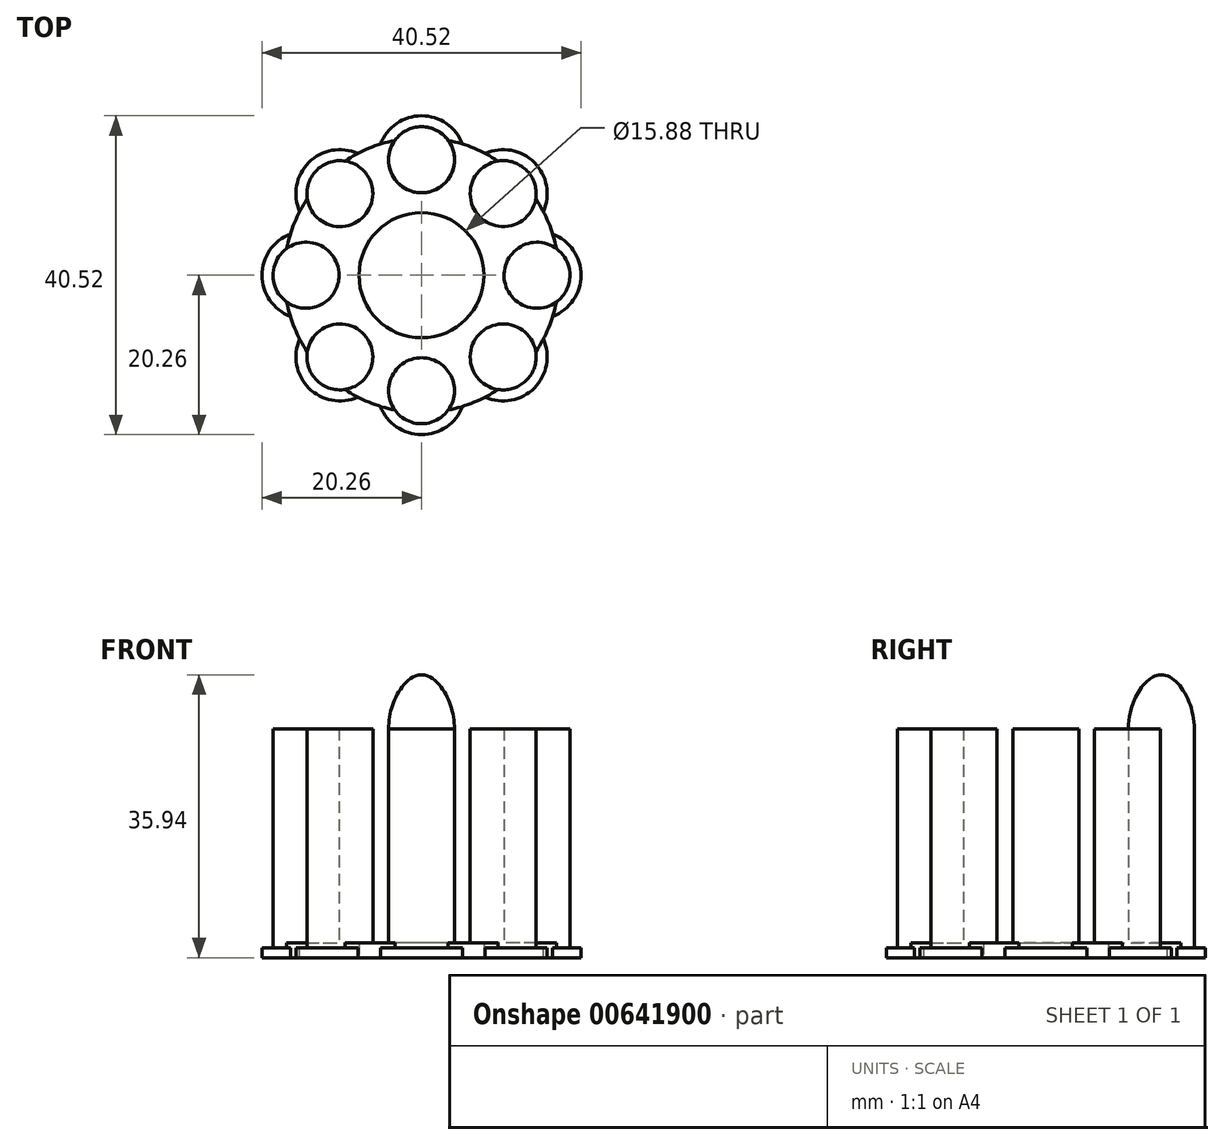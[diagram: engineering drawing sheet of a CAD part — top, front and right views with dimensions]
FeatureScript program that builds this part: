
annotation { "Feature Type Name" : "Feature", "Feature Type Description" : "" }
export const myFeature = defineFeature(function(context is Context, id is Id, definition is map)
    precondition{}
    {
        {
            var Q0;
            Q0=qCreatedBy(makeId("Top.planeOp"),FACE);
            var sketch = newSketch(context, id + "F0", { "sketchPlane" : qUnion([Q0])});
            skCircle(sketch, "E0", {"center": v(0, 14.67) * mm, "radius": 5.59 * mm});
            skCircle(sketch, "E1", {"center": v(0, 0) * mm, "radius": 7.94 * mm});
            skCircle(sketch, "E2", {"center": v(0, 14.67) * mm, "radius": 4.2 * mm});
            skCircle(sketch, "E3", {"center": v(0, 0) * mm, "radius": 17.46 * mm});
            skCircle(sketch, "E4.1.0", {"center": v(-10.37, 10.37) * mm, "radius": 4.2 * mm});
            skCircle(sketch, "E4.1.1", {"center": v(-10.37, 10.37) * mm, "radius": 5.59 * mm});
            skCircle(sketch, "E4.2.0", {"center": v(-14.67, 0) * mm, "radius": 4.2 * mm});
            skCircle(sketch, "E4.2.1", {"center": v(-14.67, 0) * mm, "radius": 5.59 * mm});
            skCircle(sketch, "E5.1.3.0", {"center": v(-10.37, -10.37) * mm, "radius": 4.2 * mm});
            skCircle(sketch, "E5.2.3.0", {"center": v(-10.37, -10.37) * mm, "radius": 5.59 * mm});
            skCircle(sketch, "E5.1.4.0", {"center": v(0, -14.67) * mm, "radius": 4.2 * mm});
            skCircle(sketch, "E5.2.4.0", {"center": v(0, -14.67) * mm, "radius": 5.59 * mm});
            skCircle(sketch, "E5.1.5.0", {"center": v(10.37, -10.37) * mm, "radius": 4.2 * mm});
            skCircle(sketch, "E5.2.5.0", {"center": v(10.37, -10.37) * mm, "radius": 5.59 * mm});
            skCircle(sketch, "E5.1.6.0", {"center": v(14.67, 0) * mm, "radius": 4.2 * mm});
            skCircle(sketch, "E5.2.6.0", {"center": v(14.67, 0) * mm, "radius": 5.59 * mm});
            skCircle(sketch, "E5.1.7.0", {"center": v(10.37, 10.37) * mm, "radius": 4.2 * mm});
            skCircle(sketch, "E5.2.7.0", {"center": v(10.37, 10.37) * mm, "radius": 5.59 * mm});
            skSolve(sketch);
        }
        {
            var Q0;
            {var subQ0=sQuery(id+"F0.wireOp",EDGE,"E3");var subQ1=sQuery(id+"F0.wireOp",EDGE,"E0");var subQ2=makeQuery(id+"F0.imprint","INTERSECT",VERTEX,{"disambiguationData":[OD(0.0)],"derivedFrom":[subQ1,subQ0]});Q0=makeQuery(id+"F0.imprint","IMPRINT",FACE,{"disambiguationData":[TD([[makeQuery(id+"F0.imprint","IMPRINT",EDGE,{"disambiguationData":[TD([[subQ2,1.0]])],"derivedFrom":subQ1}),1.0]])]});}
            var Q1;
            {var subQ0=sQuery(id+"F0.wireOp",EDGE,"E5.2.7.0");var subQ1=sQuery(id+"F0.wireOp",EDGE,"E3");var subQ2=makeQuery(id+"F0.imprint","INTERSECT",VERTEX,{"disambiguationData":[OD(0.0)],"derivedFrom":[subQ1,subQ0]});Q1=makeQuery(id+"F0.imprint","IMPRINT",FACE,{"disambiguationData":[TD([[makeQuery(id+"F0.imprint","IMPRINT",EDGE,{"disambiguationData":[TD([[subQ2,-1.0]])],"derivedFrom":subQ1}),1.0]])]});}
            var Q2;
            {var subQ0=sQuery(id+"F0.wireOp",EDGE,"E5.2.6.0");var subQ1=sQuery(id+"F0.wireOp",EDGE,"E3");var subQ2=makeQuery(id+"F0.imprint","INTERSECT",VERTEX,{"disambiguationData":[OD(0.0)],"derivedFrom":[subQ1,subQ0]});Q2=makeQuery(id+"F0.imprint","IMPRINT",FACE,{"disambiguationData":[TD([[makeQuery(id+"F0.imprint","IMPRINT",EDGE,{"disambiguationData":[TD([[subQ2,1.0]])],"derivedFrom":subQ1}),1.0]])]});}
            var Q3;
            {var subQ0=sQuery(id+"F0.wireOp",EDGE,"E5.2.5.0");var subQ1=sQuery(id+"F0.wireOp",EDGE,"E3");var subQ2=makeQuery(id+"F0.imprint","INTERSECT",VERTEX,{"disambiguationData":[OD(0.0)],"derivedFrom":[subQ1,subQ0]});Q3=makeQuery(id+"F0.imprint","IMPRINT",FACE,{"disambiguationData":[TD([[makeQuery(id+"F0.imprint","IMPRINT",EDGE,{"disambiguationData":[TD([[subQ2,-1.0]])],"derivedFrom":subQ1}),1.0]])]});}
            var Q4;
            {var subQ0=sQuery(id+"F0.wireOp",EDGE,"E5.2.4.0");var subQ1=sQuery(id+"F0.wireOp",EDGE,"E3");var subQ2=makeQuery(id+"F0.imprint","INTERSECT",VERTEX,{"disambiguationData":[OD(0.0)],"derivedFrom":[subQ1,subQ0]});Q4=makeQuery(id+"F0.imprint","IMPRINT",FACE,{"disambiguationData":[TD([[makeQuery(id+"F0.imprint","IMPRINT",EDGE,{"disambiguationData":[TD([[subQ2,-1.0]])],"derivedFrom":subQ1}),1.0]])]});}
            var Q5;
            {var subQ0=sQuery(id+"F0.wireOp",EDGE,"E5.2.3.0");var subQ1=sQuery(id+"F0.wireOp",EDGE,"E3");var subQ2=makeQuery(id+"F0.imprint","INTERSECT",VERTEX,{"disambiguationData":[OD(0.0)],"derivedFrom":[subQ1,subQ0]});Q5=makeQuery(id+"F0.imprint","IMPRINT",FACE,{"disambiguationData":[TD([[makeQuery(id+"F0.imprint","IMPRINT",EDGE,{"disambiguationData":[TD([[subQ2,-1.0]])],"derivedFrom":subQ1}),1.0]])]});}
            var Q6;
            {var subQ0=sQuery(id+"F0.wireOp",EDGE,"E4.2.1");var subQ1=sQuery(id+"F0.wireOp",EDGE,"E3");var subQ2=makeQuery(id+"F0.imprint","INTERSECT",VERTEX,{"disambiguationData":[OD(0.0)],"derivedFrom":[subQ1,subQ0]});Q6=makeQuery(id+"F0.imprint","IMPRINT",FACE,{"disambiguationData":[TD([[makeQuery(id+"F0.imprint","IMPRINT",EDGE,{"disambiguationData":[TD([[subQ2,-1.0]])],"derivedFrom":subQ1}),1.0]])]});}
            var Q7;
            {var subQ0=sQuery(id+"F0.wireOp",EDGE,"E4.1.1");var subQ1=sQuery(id+"F0.wireOp",EDGE,"E3");var subQ2=makeQuery(id+"F0.imprint","INTERSECT",VERTEX,{"disambiguationData":[OD(0.0)],"derivedFrom":[subQ1,subQ0]});Q7=makeQuery(id+"F0.imprint","IMPRINT",FACE,{"disambiguationData":[TD([[makeQuery(id+"F0.imprint","IMPRINT",EDGE,{"disambiguationData":[TD([[subQ2,-1.0]])],"derivedFrom":subQ1}),1.0]])]});}
            var Q8;
            Q8=makeQuery(id+"F0.imprint","IMPRINT",FACE,{"disambiguationData":[TD([[makeQuery(id+"F0.imprint","IMPRINT",EDGE,{"derivedFrom":sQuery(id+"F0.wireOp",EDGE,"E1")}),-1.0]])]});
            extrude(context, id + "F1", {"entities" : qUnion([Q0, Q1, Q2, Q3, Q4, Q5, Q6, Q7, Q8]), "depth" : 0.64 * mm, "offsetDistance" : 25.4 * mm});
        }
        {
            var Q0;
            Q0 = qSketchRegion(id + "F0", true);
            var Q1;
            {var subQ0=sQuery(id+"F0.wireOp",EDGE,"E5.1.4.0");var subQ1=sQuery(id+"F0.wireOp",EDGE,"E3");var subQ2=makeQuery(id+"F0.imprint","INTERSECT",VERTEX,{"disambiguationData":[OD(0.0)],"derivedFrom":[subQ1,subQ0]});Q1=makeQuery(id+"F0.imprint","IMPRINT",FACE,{"disambiguationData":[TD([[makeQuery(id+"F0.imprint","IMPRINT",EDGE,{"disambiguationData":[TD([[subQ2,-1.0]])],"derivedFrom":subQ1}),-1.0]])]});}
            var Q2;
            {var subQ0=sQuery(id+"F0.wireOp",EDGE,"E5.1.4.0");var subQ1=sQuery(id+"F0.wireOp",EDGE,"E3");var subQ2=makeQuery(id+"F0.imprint","INTERSECT",VERTEX,{"disambiguationData":[OD(0.0)],"derivedFrom":[subQ1,subQ0]});Q2=makeQuery(id+"F0.imprint","IMPRINT",FACE,{"disambiguationData":[TD([[makeQuery(id+"F0.imprint","IMPRINT",EDGE,{"disambiguationData":[TD([[subQ2,-1.0]])],"derivedFrom":subQ1}),1.0]])]});}
            var Q3;
            {var subQ0=sQuery(id+"F0.wireOp",EDGE,"E5.1.5.0");var subQ1=sQuery(id+"F0.wireOp",EDGE,"E3");var subQ2=makeQuery(id+"F0.imprint","INTERSECT",VERTEX,{"disambiguationData":[OD(0.0)],"derivedFrom":[subQ1,subQ0]});Q3=makeQuery(id+"F0.imprint","IMPRINT",FACE,{"disambiguationData":[TD([[makeQuery(id+"F0.imprint","IMPRINT",EDGE,{"disambiguationData":[TD([[subQ2,-1.0]])],"derivedFrom":subQ1}),1.0]])]});}
            var Q4;
            {var subQ0=sQuery(id+"F0.wireOp",EDGE,"E5.1.5.0");var subQ1=sQuery(id+"F0.wireOp",EDGE,"E3");var subQ2=makeQuery(id+"F0.imprint","INTERSECT",VERTEX,{"disambiguationData":[OD(0.0)],"derivedFrom":[subQ1,subQ0]});Q4=makeQuery(id+"F0.imprint","IMPRINT",FACE,{"disambiguationData":[TD([[makeQuery(id+"F0.imprint","IMPRINT",EDGE,{"disambiguationData":[TD([[subQ2,-1.0]])],"derivedFrom":subQ1}),-1.0]])]});}
            var Q5;
            {var subQ0=sQuery(id+"F0.wireOp",EDGE,"E5.1.6.0");var subQ1=sQuery(id+"F0.wireOp",EDGE,"E3");var subQ2=makeQuery(id+"F0.imprint","INTERSECT",VERTEX,{"disambiguationData":[OD(0.0)],"derivedFrom":[subQ1,subQ0]});Q5=makeQuery(id+"F0.imprint","IMPRINT",FACE,{"disambiguationData":[TD([[makeQuery(id+"F0.imprint","IMPRINT",EDGE,{"disambiguationData":[TD([[subQ2,1.0]])],"derivedFrom":subQ1}),-1.0]])]});}
            var Q6;
            {var subQ0=sQuery(id+"F0.wireOp",EDGE,"E5.1.6.0");var subQ1=sQuery(id+"F0.wireOp",EDGE,"E3");var subQ2=makeQuery(id+"F0.imprint","INTERSECT",VERTEX,{"disambiguationData":[OD(0.0)],"derivedFrom":[subQ1,subQ0]});Q6=makeQuery(id+"F0.imprint","IMPRINT",FACE,{"disambiguationData":[TD([[makeQuery(id+"F0.imprint","IMPRINT",EDGE,{"disambiguationData":[TD([[subQ2,1.0]])],"derivedFrom":subQ1}),1.0]])]});}
            var Q7;
            {var subQ0=sQuery(id+"F0.wireOp",EDGE,"E5.1.7.0");var subQ1=sQuery(id+"F0.wireOp",EDGE,"E3");var subQ2=makeQuery(id+"F0.imprint","INTERSECT",VERTEX,{"disambiguationData":[OD(0.0)],"derivedFrom":[subQ1,subQ0]});Q7=makeQuery(id+"F0.imprint","IMPRINT",FACE,{"disambiguationData":[TD([[makeQuery(id+"F0.imprint","IMPRINT",EDGE,{"disambiguationData":[TD([[subQ2,-1.0]])],"derivedFrom":subQ1}),1.0]])]});}
            var Q8;
            {var subQ0=sQuery(id+"F0.wireOp",EDGE,"E5.1.7.0");var subQ1=sQuery(id+"F0.wireOp",EDGE,"E3");var subQ2=makeQuery(id+"F0.imprint","INTERSECT",VERTEX,{"disambiguationData":[OD(0.0)],"derivedFrom":[subQ1,subQ0]});Q8=makeQuery(id+"F0.imprint","IMPRINT",FACE,{"disambiguationData":[TD([[makeQuery(id+"F0.imprint","IMPRINT",EDGE,{"disambiguationData":[TD([[subQ2,-1.0]])],"derivedFrom":subQ1}),-1.0]])]});}
            var Q9;
            {var subQ0=sQuery(id+"F0.wireOp",EDGE,"E4.1.0");var subQ1=sQuery(id+"F0.wireOp",EDGE,"E3");var subQ2=makeQuery(id+"F0.imprint","INTERSECT",VERTEX,{"disambiguationData":[OD(0.0)],"derivedFrom":[subQ1,subQ0]});Q9=makeQuery(id+"F0.imprint","IMPRINT",FACE,{"disambiguationData":[TD([[makeQuery(id+"F0.imprint","IMPRINT",EDGE,{"disambiguationData":[TD([[subQ2,-1.0]])],"derivedFrom":subQ1}),1.0]])]});}
            var Q10;
            {var subQ0=sQuery(id+"F0.wireOp",EDGE,"E4.1.0");var subQ1=sQuery(id+"F0.wireOp",EDGE,"E3");var subQ2=makeQuery(id+"F0.imprint","INTERSECT",VERTEX,{"disambiguationData":[OD(0.0)],"derivedFrom":[subQ1,subQ0]});Q10=makeQuery(id+"F0.imprint","IMPRINT",FACE,{"disambiguationData":[TD([[makeQuery(id+"F0.imprint","IMPRINT",EDGE,{"disambiguationData":[TD([[subQ2,-1.0]])],"derivedFrom":subQ1}),-1.0]])]});}
            var Q11;
            {var subQ0=sQuery(id+"F0.wireOp",EDGE,"E4.2.0");var subQ1=sQuery(id+"F0.wireOp",EDGE,"E3");var subQ2=makeQuery(id+"F0.imprint","INTERSECT",VERTEX,{"disambiguationData":[OD(0.0)],"derivedFrom":[subQ1,subQ0]});Q11=makeQuery(id+"F0.imprint","IMPRINT",FACE,{"disambiguationData":[TD([[makeQuery(id+"F0.imprint","IMPRINT",EDGE,{"disambiguationData":[TD([[subQ2,-1.0]])],"derivedFrom":subQ1}),1.0]])]});}
            var Q12;
            {var subQ0=sQuery(id+"F0.wireOp",EDGE,"E3");var subQ1=sQuery(id+"F0.wireOp",EDGE,"E2");var subQ2=makeQuery(id+"F0.imprint","INTERSECT",VERTEX,{"disambiguationData":[OD(0.0)],"derivedFrom":[subQ1,subQ0]});Q12=makeQuery(id+"F0.imprint","IMPRINT",FACE,{"disambiguationData":[TD([[makeQuery(id+"F0.imprint","IMPRINT",EDGE,{"disambiguationData":[TD([[subQ2,1.0]])],"derivedFrom":subQ1}),1.0]])]});}
            var Q13;
            {var subQ0=sQuery(id+"F0.wireOp",EDGE,"E3");var subQ1=sQuery(id+"F0.wireOp",EDGE,"E2");var subQ2=makeQuery(id+"F0.imprint","INTERSECT",VERTEX,{"disambiguationData":[OD(0.0)],"derivedFrom":[subQ1,subQ0]});Q13=makeQuery(id+"F0.imprint","IMPRINT",FACE,{"disambiguationData":[TD([[makeQuery(id+"F0.imprint","IMPRINT",EDGE,{"disambiguationData":[TD([[subQ2,-1.0]])],"derivedFrom":subQ1}),1.0]])]});}
            var Q14;
            {var subQ0=sQuery(id+"F0.wireOp",EDGE,"E5.1.3.0");var subQ1=sQuery(id+"F0.wireOp",EDGE,"E3");var subQ2=makeQuery(id+"F0.imprint","INTERSECT",VERTEX,{"disambiguationData":[OD(0.0)],"derivedFrom":[subQ1,subQ0]});Q14=makeQuery(id+"F0.imprint","IMPRINT",FACE,{"disambiguationData":[TD([[makeQuery(id+"F0.imprint","IMPRINT",EDGE,{"disambiguationData":[TD([[subQ2,-1.0]])],"derivedFrom":subQ1}),-1.0]])]});}
            var Q15;
            {var subQ0=sQuery(id+"F0.wireOp",EDGE,"E5.1.3.0");var subQ1=sQuery(id+"F0.wireOp",EDGE,"E3");var subQ2=makeQuery(id+"F0.imprint","INTERSECT",VERTEX,{"disambiguationData":[OD(0.0)],"derivedFrom":[subQ1,subQ0]});Q15=makeQuery(id+"F0.imprint","IMPRINT",FACE,{"disambiguationData":[TD([[makeQuery(id+"F0.imprint","IMPRINT",EDGE,{"disambiguationData":[TD([[subQ2,-1.0]])],"derivedFrom":subQ1}),1.0]])]});}
            var Q16;
            {var subQ0=sQuery(id+"F0.wireOp",EDGE,"E4.2.0");var subQ1=sQuery(id+"F0.wireOp",EDGE,"E3");var subQ2=makeQuery(id+"F0.imprint","INTERSECT",VERTEX,{"disambiguationData":[OD(0.0)],"derivedFrom":[subQ1,subQ0]});Q16=makeQuery(id+"F0.imprint","IMPRINT",FACE,{"disambiguationData":[TD([[makeQuery(id+"F0.imprint","IMPRINT",EDGE,{"disambiguationData":[TD([[subQ2,-1.0]])],"derivedFrom":subQ1}),-1.0]])]});}
            extrude(context, id + "F2", {"entities" : qUnion([Q0, Q1, Q2, Q3, Q4, Q5, Q6, Q7, Q8, Q9, Q10, Q11, Q12, Q13, Q14, Q15, Q16]), "operationType" : NewBodyOperationType.ADD, "oppositeDirection" : true, "depth" : 1.27 * mm, "offsetDistance" : 25.4 * mm});
        }
        {
            var Q0;
            {var subQ0=sQuery(id+"F0.wireOp",EDGE,"E5.1.5.0");var subQ1=sQuery(id+"F0.wireOp",EDGE,"E3");var subQ2=makeQuery(id+"F0.imprint","INTERSECT",VERTEX,{"disambiguationData":[OD(0.0)],"derivedFrom":[subQ1,subQ0]});Q0=makeQuery(id+"F0.imprint","IMPRINT",FACE,{"disambiguationData":[TD([[makeQuery(id+"F0.imprint","IMPRINT",EDGE,{"disambiguationData":[TD([[subQ2,-1.0]])],"derivedFrom":subQ1}),1.0]])]});}
            var Q1;
            {var subQ0=sQuery(id+"F0.wireOp",EDGE,"E5.1.5.0");var subQ1=sQuery(id+"F0.wireOp",EDGE,"E3");var subQ2=makeQuery(id+"F0.imprint","INTERSECT",VERTEX,{"disambiguationData":[OD(0.0)],"derivedFrom":[subQ1,subQ0]});Q1=makeQuery(id+"F0.imprint","IMPRINT",FACE,{"disambiguationData":[TD([[makeQuery(id+"F0.imprint","IMPRINT",EDGE,{"disambiguationData":[TD([[subQ2,-1.0]])],"derivedFrom":subQ1}),-1.0]])]});}
            var Q2;
            {var subQ0=sQuery(id+"F0.wireOp",EDGE,"E5.1.4.0");var subQ1=sQuery(id+"F0.wireOp",EDGE,"E3");var subQ2=makeQuery(id+"F0.imprint","INTERSECT",VERTEX,{"disambiguationData":[OD(0.0)],"derivedFrom":[subQ1,subQ0]});Q2=makeQuery(id+"F0.imprint","IMPRINT",FACE,{"disambiguationData":[TD([[makeQuery(id+"F0.imprint","IMPRINT",EDGE,{"disambiguationData":[TD([[subQ2,-1.0]])],"derivedFrom":subQ1}),-1.0]])]});}
            var Q3;
            {var subQ0=sQuery(id+"F0.wireOp",EDGE,"E5.1.4.0");var subQ1=sQuery(id+"F0.wireOp",EDGE,"E3");var subQ2=makeQuery(id+"F0.imprint","INTERSECT",VERTEX,{"disambiguationData":[OD(0.0)],"derivedFrom":[subQ1,subQ0]});Q3=makeQuery(id+"F0.imprint","IMPRINT",FACE,{"disambiguationData":[TD([[makeQuery(id+"F0.imprint","IMPRINT",EDGE,{"disambiguationData":[TD([[subQ2,-1.0]])],"derivedFrom":subQ1}),1.0]])]});}
            var Q4;
            {var subQ0=sQuery(id+"F0.wireOp",EDGE,"E5.1.3.0");var subQ1=sQuery(id+"F0.wireOp",EDGE,"E3");var subQ2=makeQuery(id+"F0.imprint","INTERSECT",VERTEX,{"disambiguationData":[OD(0.0)],"derivedFrom":[subQ1,subQ0]});Q4=makeQuery(id+"F0.imprint","IMPRINT",FACE,{"disambiguationData":[TD([[makeQuery(id+"F0.imprint","IMPRINT",EDGE,{"disambiguationData":[TD([[subQ2,-1.0]])],"derivedFrom":subQ1}),1.0]])]});}
            var Q5;
            {var subQ0=sQuery(id+"F0.wireOp",EDGE,"E5.1.3.0");var subQ1=sQuery(id+"F0.wireOp",EDGE,"E3");var subQ2=makeQuery(id+"F0.imprint","INTERSECT",VERTEX,{"disambiguationData":[OD(0.0)],"derivedFrom":[subQ1,subQ0]});Q5=makeQuery(id+"F0.imprint","IMPRINT",FACE,{"disambiguationData":[TD([[makeQuery(id+"F0.imprint","IMPRINT",EDGE,{"disambiguationData":[TD([[subQ2,-1.0]])],"derivedFrom":subQ1}),-1.0]])]});}
            var Q6;
            {var subQ0=sQuery(id+"F0.wireOp",EDGE,"E4.2.0");var subQ1=sQuery(id+"F0.wireOp",EDGE,"E3");var subQ2=makeQuery(id+"F0.imprint","INTERSECT",VERTEX,{"disambiguationData":[OD(0.0)],"derivedFrom":[subQ1,subQ0]});Q6=makeQuery(id+"F0.imprint","IMPRINT",FACE,{"disambiguationData":[TD([[makeQuery(id+"F0.imprint","IMPRINT",EDGE,{"disambiguationData":[TD([[subQ2,-1.0]])],"derivedFrom":subQ1}),1.0]])]});}
            var Q7;
            {var subQ0=sQuery(id+"F0.wireOp",EDGE,"E4.2.0");var subQ1=sQuery(id+"F0.wireOp",EDGE,"E3");var subQ2=makeQuery(id+"F0.imprint","INTERSECT",VERTEX,{"disambiguationData":[OD(0.0)],"derivedFrom":[subQ1,subQ0]});Q7=makeQuery(id+"F0.imprint","IMPRINT",FACE,{"disambiguationData":[TD([[makeQuery(id+"F0.imprint","IMPRINT",EDGE,{"disambiguationData":[TD([[subQ2,-1.0]])],"derivedFrom":subQ1}),-1.0]])]});}
            var Q8;
            {var subQ0=sQuery(id+"F0.wireOp",EDGE,"E4.1.0");var subQ1=sQuery(id+"F0.wireOp",EDGE,"E3");var subQ2=makeQuery(id+"F0.imprint","INTERSECT",VERTEX,{"disambiguationData":[OD(0.0)],"derivedFrom":[subQ1,subQ0]});Q8=makeQuery(id+"F0.imprint","IMPRINT",FACE,{"disambiguationData":[TD([[makeQuery(id+"F0.imprint","IMPRINT",EDGE,{"disambiguationData":[TD([[subQ2,-1.0]])],"derivedFrom":subQ1}),1.0]])]});}
            var Q9;
            {var subQ0=sQuery(id+"F0.wireOp",EDGE,"E4.1.0");var subQ1=sQuery(id+"F0.wireOp",EDGE,"E3");var subQ2=makeQuery(id+"F0.imprint","INTERSECT",VERTEX,{"disambiguationData":[OD(0.0)],"derivedFrom":[subQ1,subQ0]});Q9=makeQuery(id+"F0.imprint","IMPRINT",FACE,{"disambiguationData":[TD([[makeQuery(id+"F0.imprint","IMPRINT",EDGE,{"disambiguationData":[TD([[subQ2,-1.0]])],"derivedFrom":subQ1}),-1.0]])]});}
            var Q10;
            {var subQ0=sQuery(id+"F0.wireOp",EDGE,"E3");var subQ1=sQuery(id+"F0.wireOp",EDGE,"E2");var subQ2=makeQuery(id+"F0.imprint","INTERSECT",VERTEX,{"disambiguationData":[OD(0.0)],"derivedFrom":[subQ1,subQ0]});Q10=makeQuery(id+"F0.imprint","IMPRINT",FACE,{"disambiguationData":[TD([[makeQuery(id+"F0.imprint","IMPRINT",EDGE,{"disambiguationData":[TD([[subQ2,1.0]])],"derivedFrom":subQ1}),1.0]])]});}
            var Q11;
            {var subQ0=sQuery(id+"F0.wireOp",EDGE,"E3");var subQ1=sQuery(id+"F0.wireOp",EDGE,"E2");var subQ2=makeQuery(id+"F0.imprint","INTERSECT",VERTEX,{"disambiguationData":[OD(0.0)],"derivedFrom":[subQ1,subQ0]});Q11=makeQuery(id+"F0.imprint","IMPRINT",FACE,{"disambiguationData":[TD([[makeQuery(id+"F0.imprint","IMPRINT",EDGE,{"disambiguationData":[TD([[subQ2,-1.0]])],"derivedFrom":subQ1}),1.0]])]});}
            var Q12;
            {var subQ0=sQuery(id+"F0.wireOp",EDGE,"E5.1.7.0");var subQ1=sQuery(id+"F0.wireOp",EDGE,"E3");var subQ2=makeQuery(id+"F0.imprint","INTERSECT",VERTEX,{"disambiguationData":[OD(0.0)],"derivedFrom":[subQ1,subQ0]});Q12=makeQuery(id+"F0.imprint","IMPRINT",FACE,{"disambiguationData":[TD([[makeQuery(id+"F0.imprint","IMPRINT",EDGE,{"disambiguationData":[TD([[subQ2,-1.0]])],"derivedFrom":subQ1}),1.0]])]});}
            var Q13;
            {var subQ0=sQuery(id+"F0.wireOp",EDGE,"E5.1.7.0");var subQ1=sQuery(id+"F0.wireOp",EDGE,"E3");var subQ2=makeQuery(id+"F0.imprint","INTERSECT",VERTEX,{"disambiguationData":[OD(0.0)],"derivedFrom":[subQ1,subQ0]});Q13=makeQuery(id+"F0.imprint","IMPRINT",FACE,{"disambiguationData":[TD([[makeQuery(id+"F0.imprint","IMPRINT",EDGE,{"disambiguationData":[TD([[subQ2,-1.0]])],"derivedFrom":subQ1}),-1.0]])]});}
            var Q14;
            {var subQ0=sQuery(id+"F0.wireOp",EDGE,"E5.1.6.0");var subQ1=sQuery(id+"F0.wireOp",EDGE,"E3");var subQ2=makeQuery(id+"F0.imprint","INTERSECT",VERTEX,{"disambiguationData":[OD(0.0)],"derivedFrom":[subQ1,subQ0]});Q14=makeQuery(id+"F0.imprint","IMPRINT",FACE,{"disambiguationData":[TD([[makeQuery(id+"F0.imprint","IMPRINT",EDGE,{"disambiguationData":[TD([[subQ2,1.0]])],"derivedFrom":subQ1}),1.0]])]});}
            var Q15;
            {var subQ0=sQuery(id+"F0.wireOp",EDGE,"E5.1.6.0");var subQ1=sQuery(id+"F0.wireOp",EDGE,"E3");var subQ2=makeQuery(id+"F0.imprint","INTERSECT",VERTEX,{"disambiguationData":[OD(0.0)],"derivedFrom":[subQ1,subQ0]});Q15=makeQuery(id+"F0.imprint","IMPRINT",FACE,{"disambiguationData":[TD([[makeQuery(id+"F0.imprint","IMPRINT",EDGE,{"disambiguationData":[TD([[subQ2,1.0]])],"derivedFrom":subQ1}),-1.0]])]});}
            extrude(context, id + "F3", {"entities" : qUnion([Q0, Q1, Q2, Q3, Q4, Q5, Q6, Q7, Q8, Q9, Q10, Q11, Q12, Q13, Q14, Q15]), "operationType" : NewBodyOperationType.ADD, "depth" : 27.8 * mm, "offsetDistance" : 25.4 * mm});
        }
        {
            var Q0;
            Q0=qCreatedBy(makeId("Right.planeOp"),FACE);
            var sketch = newSketch(context, id + "F4", { "sketchPlane" : qUnion([Q0])});
            skLineSegment(sketch, "E6", {"start": v(14.67, 27.81) * mm, "end": v(14.67, 34.67) * mm});
            skFitSpline(sketch, "E7", {"points": [v(14.67, 34.67) * mm, v(18.86, 27.81) * mm], "startDerivative": vector(6.29, 0) * mm, "endDerivative": vector(0, -10.29) * mm});
            skLineSegment(sketch, "E8", {"start": v(18.86, 27.81) * mm, "end": v(14.67, 27.81) * mm});
            skLineSegment(sketch, "E9", {"start": v(0, 0) * mm, "end": v(0, 29.34) * mm, "construction": true});
            skPoint(sketch, "E10", {"position": v(14.67, 31.24) * mm});
            skLineSegment(sketch, "E11", {"start": v(25.4, -1.27) * mm, "end": v(25.4, 34.67) * mm, "construction": true});
            skPoint(sketch, "E12", {"position": v(16.76, 27.81) * mm});
            skSolve(sketch);
        }
        {
            var Q0;
            Q0=makeQuery(id+"F4.imprint","IMPRINT",FACE,{"disambiguationData":[TD([[makeQuery(id+"F4.imprint","IMPRINT",EDGE,{"derivedFrom":sQuery(id+"F4.wireOp",EDGE,"E6")}),-1.0]])]});
            var Q1;
            Q1=sQuery(id+"F4.wireOp",EDGE,"E6");
            revolve(context, id + "F5", {"operationType" : NewBodyOperationType.ADD, "entities" : qUnion([Q0]), "axis" : qUnion([Q1]), "revolveType" : RevolveType.FULL});
        }
    });
